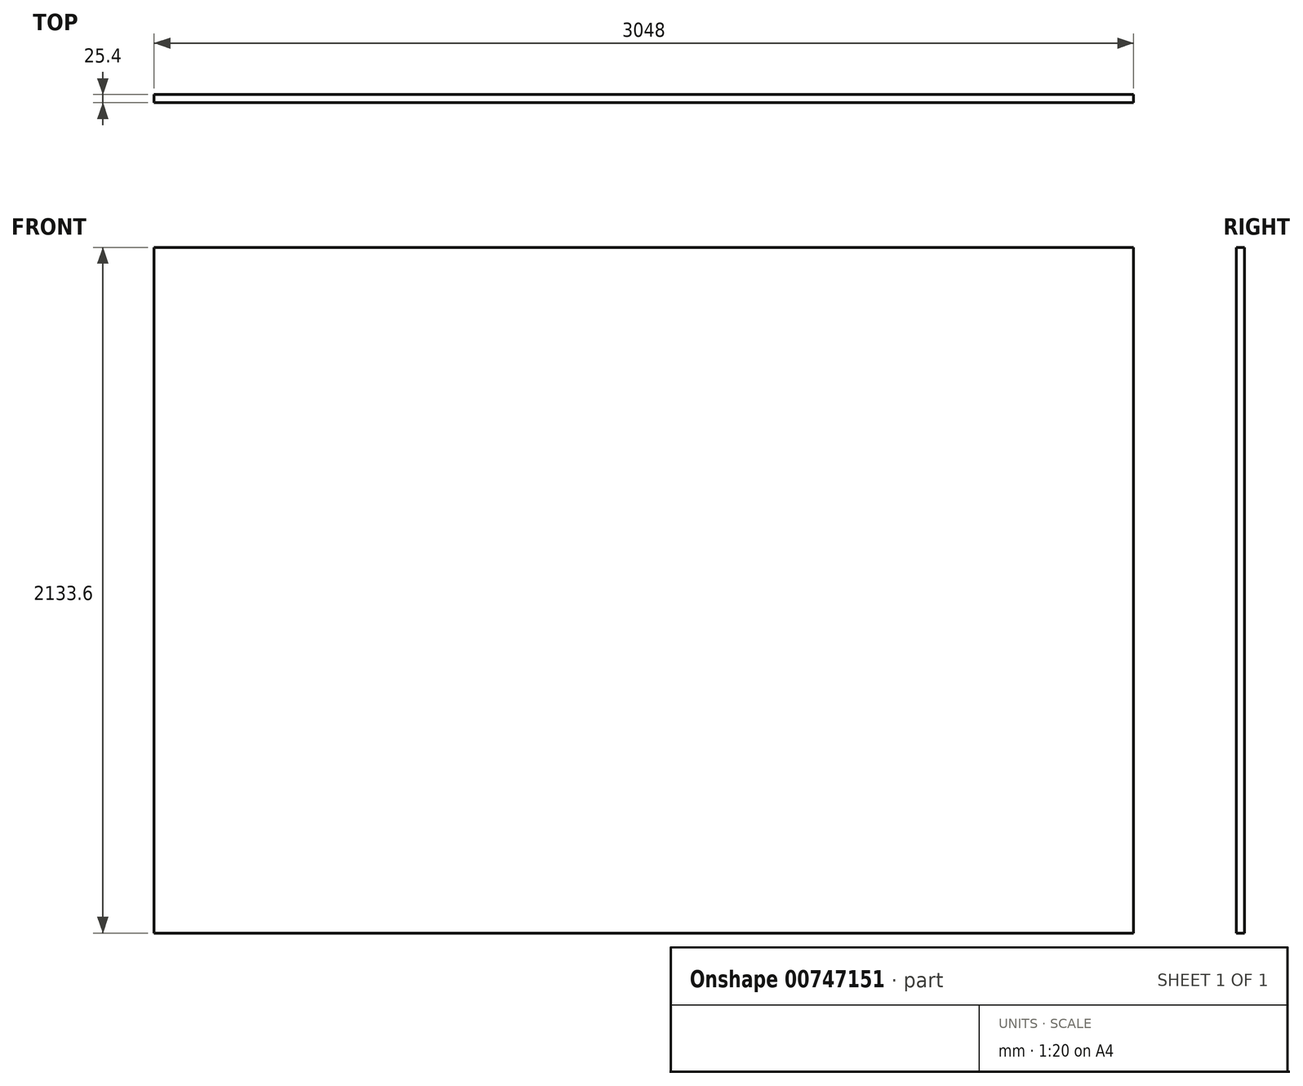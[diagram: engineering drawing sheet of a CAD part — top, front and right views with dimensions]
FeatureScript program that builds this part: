
annotation { "Feature Type Name" : "Feature", "Feature Type Description" : "" }
export const myFeature = defineFeature(function(context is Context, id is Id, definition is map)
    precondition{}
    {
        {
            var Q0;
            Q0=qCreatedBy(makeId("Right.planeOp"),FACE);
            var sketch = newSketch(context, id + "F0", { "sketchPlane" : qUnion([Q0])});
            skLineSegment(sketch, "E0.bottom", {"start": v(-25.4, 2048.56) * mm, "end": v(0, 2048.56) * mm});
            skLineSegment(sketch, "E0.top", {"start": v(-25.4, -85.04) * mm, "end": v(0, -85.04) * mm});
            skLineSegment(sketch, "E0.left", {"start": v(-25.4, 2048.56) * mm, "end": v(-25.4, -85.04) * mm});
            skLineSegment(sketch, "E0.right", {"start": v(0, 2048.56) * mm, "end": v(0, -85.04) * mm});
            skSolve(sketch);
        }
        {
            var Q0;
            Q0 = qSketchRegion(id + "F0", true);
            extrude(context, id + "F1", {"entities" : qUnion([Q0]), "oppositeDirection" : true, "depth" : 3048 * mm, "offsetDistance" : 25.4 * mm});
        }
    });
